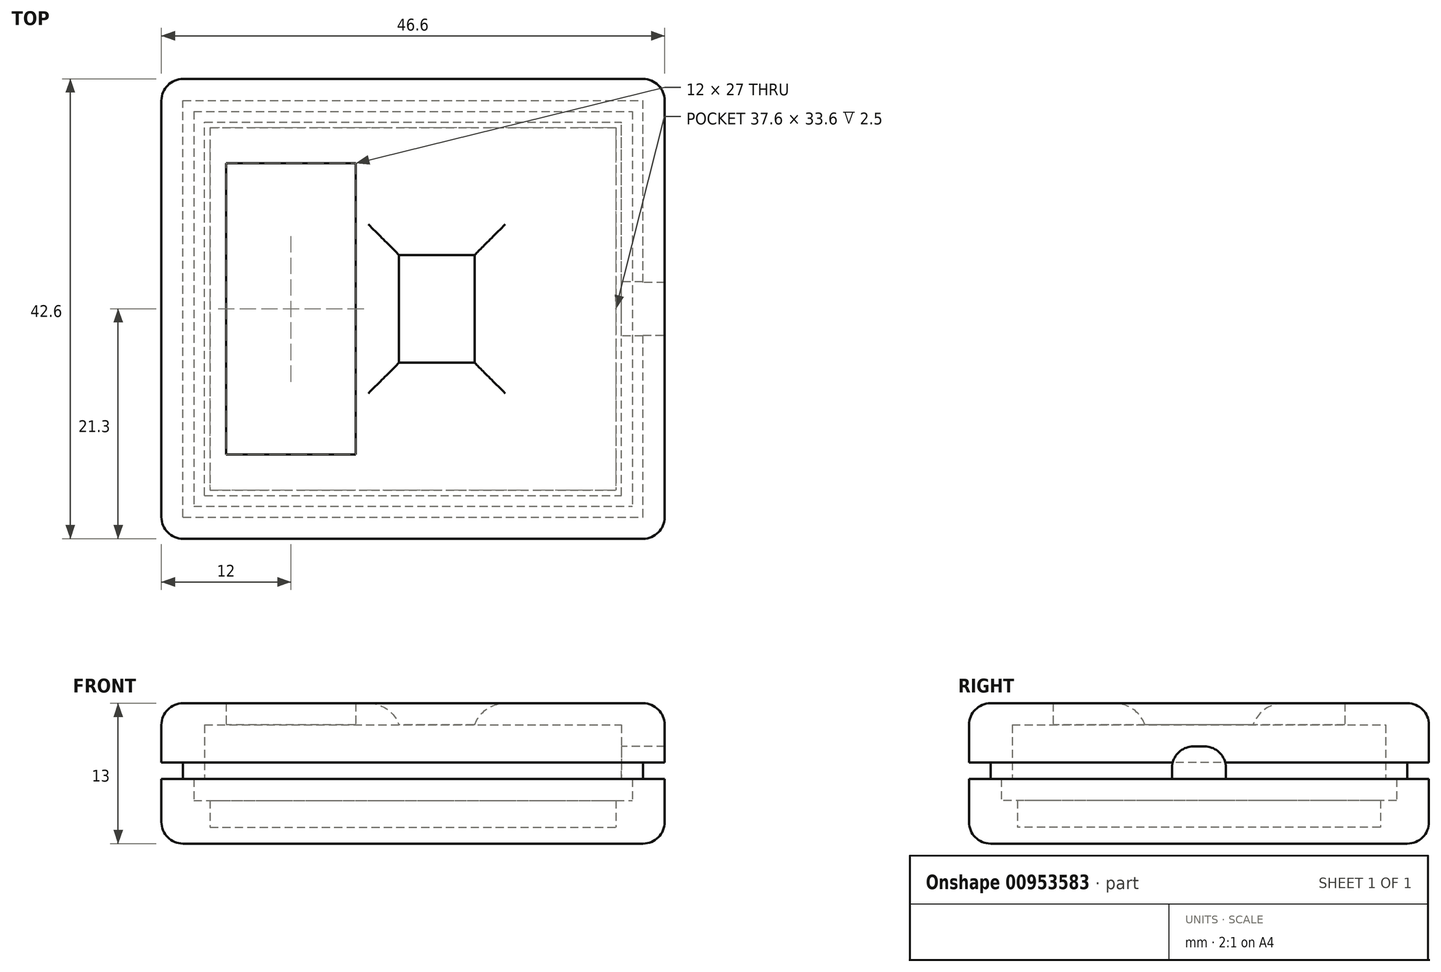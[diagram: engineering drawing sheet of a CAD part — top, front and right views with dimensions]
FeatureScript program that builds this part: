
annotation { "Feature Type Name" : "Feature", "Feature Type Description" : "" }
export const myFeature = defineFeature(function(context is Context, id is Id, definition is map)
    precondition{}
    {
        {
            assignVariable(context, id + "F0", {"name" : "HIGH", "anyValue" : 6 * mm});
        }
        {
            assignVariable(context, id + "F1", {"name" : "PCB_HIGH", "anyValue" : 2 * mm});
        }
        {
            var Q0;
            Q0=qCreatedBy(makeId("Top.planeOp"),FACE);
            var sketch = newSketch(context, id + "F2", { "sketchPlane" : qUnion([Q0])});
            skLineSegment(sketch, "E0.bottom", {"start": v(-23.3, 21.3) * mm, "end": v(23.3, 21.3) * mm});
            skLineSegment(sketch, "E0.top", {"start": v(-23.3, -21.3) * mm, "end": v(23.3, -21.3) * mm});
            skLineSegment(sketch, "E0.left", {"start": v(-23.3, 21.3) * mm, "end": v(-23.3, -21.3) * mm});
            skLineSegment(sketch, "E0.right", {"start": v(23.3, 21.3) * mm, "end": v(23.3, -21.3) * mm});
            skLineSegment(sketch, "E1", {"start": v(-23.3, 21.3) * mm, "end": v(23.3, -21.3) * mm, "construction": true});
            skLineSegment(sketch, "E2", {"start": v(23.3, 21.3) * mm, "end": v(-23.3, -21.3) * mm, "construction": true});
            skPoint(sketch, "E3", {"position": v(0, 0) * mm});
            skSolve(sketch);
        }
        {
            var Q0;
            Q0=qSketchRegion(id+"F2",true);
            extrude(context, id + "F3", {"entities" : qUnion([Q0]), "depth" : (getVariable(context, 'HIGH')), "offsetDistance" : 25 * mm});
        }
        {
            var Q0;
            Q0=qCreatedBy(makeId("Top.planeOp"),FACE);
            cPlane(context, id + "F4", {"entities" : qUnion([Q0]), "cplaneType" : CPlaneType.OFFSET, "offset" : 1.5 * mm, "width" : 150 * mm, "height" : 150 * mm});
        }
        {
            var Q0;
            Q0=qCreatedBy(id+"F4.planeOp",FACE);
            var sketch = newSketch(context, id + "F5", { "sketchPlane" : qUnion([Q0])});
            skLineSegment(sketch, "E4.bottom", {"start": v(-18.8, 16.8) * mm, "end": v(18.8, 16.8) * mm});
            skLineSegment(sketch, "E4.top", {"start": v(-18.8, -16.8) * mm, "end": v(18.8, -16.8) * mm});
            skLineSegment(sketch, "E4.left", {"start": v(-18.8, 16.8) * mm, "end": v(-18.8, -16.8) * mm});
            skLineSegment(sketch, "E4.right", {"start": v(18.8, 16.8) * mm, "end": v(18.8, -16.8) * mm});
            skSolve(sketch);
        }
        {
            var Q0;
            Q0=qSketchRegion(id+"F5",true);
            extrude(context, id + "F6", {"entities" : qUnion([Q0]), "operationType" : NewBodyOperationType.REMOVE, "depth" : (getVariable(context, 'HIGH') - 1.5 * mm), "offsetDistance" : 25 * mm});
        }
        {
            var Q0;
            Q0=qCreatedBy(makeId("Top.planeOp"),FACE);
            cPlane(context, id + "F7", {"entities" : qUnion([Q0]), "cplaneType" : CPlaneType.OFFSET, "offset" : (getVariable(context, 'HIGH') - getVariable(context, 'PCB_HIGH')), "width" : 150 * mm, "height" : 150 * mm});
        }
        {
            var Q0;
            Q0=qCreatedBy(id+"F7.planeOp",FACE);
            var sketch = newSketch(context, id + "F8", { "sketchPlane" : qUnion([Q0])});
            skLineSegment(sketch, "E5.bottom", {"start": v(-18.8, 16.8) * mm, "end": v(18.8, 16.8) * mm});
            skLineSegment(sketch, "E5.top", {"start": v(-18.8, -16.8) * mm, "end": v(18.8, -16.8) * mm});
            skLineSegment(sketch, "E5.left", {"start": v(-18.8, 16.8) * mm, "end": v(-18.8, -16.8) * mm});
            skLineSegment(sketch, "E5.right", {"start": v(18.8, 16.8) * mm, "end": v(18.8, -16.8) * mm});
            skLineSegment(sketch, "E6.bottom", {"start": v(-20.3, 18.3) * mm, "end": v(20.3, 18.3) * mm});
            skLineSegment(sketch, "E6.top", {"start": v(-20.3, -18.3) * mm, "end": v(20.3, -18.3) * mm});
            skLineSegment(sketch, "E6.left", {"start": v(-20.3, 18.3) * mm, "end": v(-20.3, -18.3) * mm});
            skLineSegment(sketch, "E6.right", {"start": v(20.3, 18.3) * mm, "end": v(20.3, -18.3) * mm});
            skSolve(sketch);
        }
        {
            var Q0;
            Q0=qSketchRegion(id+"F8",true);
            extrude(context, id + "F9", {"entities" : qUnion([Q0]), "operationType" : NewBodyOperationType.REMOVE, "depth" : (getVariable(context, 'PCB_HIGH')), "offsetDistance" : 25 * mm});
        }
        {
            var Q0;
            Q0=makeQuery(id+"F3.opExtrude","CAP_FACE",FACE,{"disambiguationData":[OSD([sQuery(id+"F2.wireOp",EDGE,"E0.bottom"),sQuery(id+"F2.wireOp",EDGE,"E0.top"),sQuery(id+"F2.wireOp",EDGE,"E0.left"),sQuery(id+"F2.wireOp",EDGE,"E0.right")])],"isStart":false});
            var sketch = newSketch(context, id + "F10", { "sketchPlane" : qUnion([Q0])});
            skLineSegment(sketch, "E7.bottom", {"start": v(-23.3, 21.3) * mm, "end": v(23.3, 21.3) * mm});
            skLineSegment(sketch, "E7.top", {"start": v(-23.3, -21.3) * mm, "end": v(23.3, -21.3) * mm});
            skLineSegment(sketch, "E7.left", {"start": v(-23.3, 21.3) * mm, "end": v(-23.3, -21.3) * mm});
            skLineSegment(sketch, "E7.right", {"start": v(23.3, 21.3) * mm, "end": v(23.3, -21.3) * mm});
            skLineSegment(sketch, "E8.bottom", {"start": v(-21.8, 19.8) * mm, "end": v(21.8, 19.8) * mm});
            skLineSegment(sketch, "E8.top", {"start": v(-21.8, -19.8) * mm, "end": v(21.8, -19.8) * mm});
            skLineSegment(sketch, "E8.left", {"start": v(-21.8, 19.8) * mm, "end": v(-21.8, -19.8) * mm});
            skLineSegment(sketch, "E8.right", {"start": v(21.8, 19.8) * mm, "end": v(21.8, -19.8) * mm});
            skSolve(sketch);
        }
        {
            var Q0;
            Q0 = qSketchRegion(id + "F10", true);
            extrude(context, id + "F11", {"entities" : qUnion([Q0]), "operationType" : NewBodyOperationType.ADD, "depth" : 1.5 * mm, "offsetDistance" : 25 * mm});
        }
        {
            var Q0;
            Q0=makeQuery(id+"F11.boolean.opBoolean","MERGE",EDGE,{"derivedFrom":[makeQuery(id+"F3.opExtrude","SWEPT_EDGE",EDGE,{"disambiguationData":[OSD([sQuery(id+"F2.wireOp",EDGE,"E0.bottom"),sQuery(id+"F2.wireOp",EDGE,"E0.left")])]}),makeQuery(id+"F11.opExtrude","SWEPT_EDGE",EDGE,{"disambiguationData":[OSD([sQuery(id+"F10.wireOp",EDGE,"E7.bottom"),sQuery(id+"F10.wireOp",EDGE,"E7.left")])]})]});
            var Q1;
            Q1=makeQuery(id+"F11.boolean.opBoolean","MERGE",EDGE,{"derivedFrom":[makeQuery(id+"F3.opExtrude","SWEPT_EDGE",EDGE,{"disambiguationData":[OSD([sQuery(id+"F2.wireOp",EDGE,"E0.top"),sQuery(id+"F2.wireOp",EDGE,"E0.left")])]}),makeQuery(id+"F11.opExtrude","SWEPT_EDGE",EDGE,{"disambiguationData":[OSD([sQuery(id+"F10.wireOp",EDGE,"E7.top"),sQuery(id+"F10.wireOp",EDGE,"E7.left")])]})]});
            var Q2;
            Q2=makeQuery(id+"F11.boolean.opBoolean","MERGE",EDGE,{"derivedFrom":[makeQuery(id+"F3.opExtrude","SWEPT_EDGE",EDGE,{"disambiguationData":[OSD([sQuery(id+"F2.wireOp",EDGE,"E0.bottom"),sQuery(id+"F2.wireOp",EDGE,"E0.right")])]}),makeQuery(id+"F11.opExtrude","SWEPT_EDGE",EDGE,{"disambiguationData":[OSD([sQuery(id+"F10.wireOp",EDGE,"E7.bottom"),sQuery(id+"F10.wireOp",EDGE,"E7.right")])]})]});
            var Q3;
            Q3=makeQuery(id+"F11.boolean.opBoolean","MERGE",EDGE,{"derivedFrom":[makeQuery(id+"F3.opExtrude","SWEPT_EDGE",EDGE,{"disambiguationData":[OSD([sQuery(id+"F2.wireOp",EDGE,"E0.top"),sQuery(id+"F2.wireOp",EDGE,"E0.right")])]}),makeQuery(id+"F11.opExtrude","SWEPT_EDGE",EDGE,{"disambiguationData":[OSD([sQuery(id+"F10.wireOp",EDGE,"E7.top"),sQuery(id+"F10.wireOp",EDGE,"E7.right")])]})]});
            fillet(context, id + "F12", {"entities" : qUnion([Q0, Q1, Q2, Q3]), "radius" : 2 * mm, "tangentPropagation" : true, "allowEdgeOverflow" : false});
        }
        {
            var Q0;
            Q0=makeQuery(id+"F11.opExtrude","CAP_FACE",FACE,{"disambiguationData":[OSD([sQuery(id+"F10.wireOp",EDGE,"E7.bottom"),sQuery(id+"F10.wireOp",EDGE,"E7.top"),sQuery(id+"F10.wireOp",EDGE,"E7.left"),sQuery(id+"F10.wireOp",EDGE,"E7.right"),sQuery(id+"F10.wireOp",EDGE,"E8.bottom"),sQuery(id+"F10.wireOp",EDGE,"E8.top"),sQuery(id+"F10.wireOp",EDGE,"E8.left"),sQuery(id+"F10.wireOp",EDGE,"E8.right")])],"isStart":false});
            var sketch = newSketch(context, id + "F13", { "sketchPlane" : qUnion([Q0])});
            skLineSegment(sketch, "E9.bottom", {"start": v(21.8, 2.5) * mm, "end": v(23.3, 2.5) * mm});
            skLineSegment(sketch, "E9.top", {"start": v(21.8, -2.5) * mm, "end": v(23.3, -2.5) * mm});
            skLineSegment(sketch, "E9.left", {"start": v(21.8, 2.5) * mm, "end": v(21.8, -2.5) * mm});
            skLineSegment(sketch, "E9.right", {"start": v(23.3, 2.5) * mm, "end": v(23.3, -2.5) * mm});
            skLineSegment(sketch, "E10", {"start": v(-25.81, 0) * mm, "end": v(25.62, 0) * mm, "construction": true});
            skPoint(sketch, "E10.endSnap0", {"position": v(23.3, 0) * mm});
            skSolve(sketch);
        }
        {
            var Q0;
            Q0 = qSketchRegion(id + "F13", true);
            extrude(context, id + "F14", {"entities" : qUnion([Q0]), "operationType" : NewBodyOperationType.REMOVE, "oppositeDirection" : true, "depth" : 1.5 * mm, "offsetDistance" : 25 * mm});
        }
        {
            var Q0;
            Q0=makeQuery(id+"F14.boolean.opBoolean","COPY",EDGE,{"derivedFrom":makeQuery(id+"F14.opExtrude","CAP_EDGE",EDGE,{"disambiguationData":[OSD([sQuery(id+"F13.wireOp",EDGE,"E9.top")])],"isStart":false})});
            var Q1;
            Q1=makeQuery(id+"F14.boolean.opBoolean","COPY",EDGE,{"derivedFrom":makeQuery(id+"F14.opExtrude","CAP_EDGE",EDGE,{"disambiguationData":[OSD([sQuery(id+"F13.wireOp",EDGE,"E9.bottom")])],"isStart":false})});
            fillet(context, id + "F15", {"entities" : qUnion([Q0, Q1]), "radius" : 2 * mm, "tangentPropagation" : true, "allowEdgeOverflow" : false});
        }
        {
            var Q0;
            Q0=makeQuery(id+"F3.opExtrude","CAP_EDGE",EDGE,{"disambiguationData":[OSD([sQuery(id+"F2.wireOp",EDGE,"E0.left")])],"isStart":true});
            fillet(context, id + "F16", {"entities" : qUnion([Q0]), "radius" : 2 * mm, "tangentPropagation" : true, "allowEdgeOverflow" : false});
        }
        {
            var Q0;
            Q0=makeQuery(id+"F3.opExtrude","CAP_FACE",FACE,{"disambiguationData":[OSD([sQuery(id+"F2.wireOp",EDGE,"E0.bottom"),sQuery(id+"F2.wireOp",EDGE,"E0.top"),sQuery(id+"F2.wireOp",EDGE,"E0.left"),sQuery(id+"F2.wireOp",EDGE,"E0.right")])],"isStart":false});
            cPlane(context, id + "F17", {"entities" : qUnion([Q0]), "cplaneType" : CPlaneType.OFFSET, "offset" : 0 * mm, "width" : 150 * mm, "height" : 150 * mm});
        }
        {
            var Q0;
            Q0=qCreatedBy(id+"F17.planeOp",FACE);
            var sketch = newSketch(context, id + "F18", { "sketchPlane" : qUnion([Q0])});
            skLineSegment(sketch, "E11.bottom", {"start": v(-23.3, 21.3) * mm, "end": v(23.3, 21.3) * mm});
            skLineSegment(sketch, "E11.top", {"start": v(-23.3, -21.3) * mm, "end": v(23.3, -21.3) * mm});
            skLineSegment(sketch, "E11.left", {"start": v(-23.3, 21.3) * mm, "end": v(-23.3, -21.3) * mm});
            skLineSegment(sketch, "E11.right", {"start": v(23.3, 21.3) * mm, "end": v(23.3, -21.3) * mm});
            skSolve(sketch);
        }
        {
            var Q0;
            Q0=qSketchRegion(id+"F18",true);
            extrude(context, id + "F19", {"entities" : qUnion([Q0]), "depth" : (5 + 2) * mm, "offsetDistance" : 25 * mm});
        }
        {
            var Q0;
            Q0=qCreatedBy(id+"F17.planeOp",FACE);
            var sketch = newSketch(context, id + "F20", { "sketchPlane" : qUnion([Q0])});
            skLineSegment(sketch, "E12.bottom", {"start": v(-19.3, -17.3) * mm, "end": v(19.3, -17.3) * mm});
            skLineSegment(sketch, "E12.top", {"start": v(-19.3, 17.3) * mm, "end": v(19.3, 17.3) * mm});
            skLineSegment(sketch, "E12.left", {"start": v(-19.3, -17.3) * mm, "end": v(-19.3, 17.3) * mm});
            skLineSegment(sketch, "E12.right", {"start": v(19.3, -17.3) * mm, "end": v(19.3, 17.3) * mm});
            skSolve(sketch);
        }
        {
            var Q0;
            Q0=qSketchRegion(id+"F20",true);
            extrude(context, id + "F21", {"entities" : qUnion([Q0]), "operationType" : NewBodyOperationType.REMOVE, "depth" : 5 * mm, "offsetDistance" : 25 * mm});
        }
        {
            var Q0;
            Q0=makeQuery(id+"F19.opExtrude","CAP_FACE",FACE,{"disambiguationData":[OSD([sQuery(id+"F18.wireOp",EDGE,"E11.bottom"),sQuery(id+"F18.wireOp",EDGE,"E11.top"),sQuery(id+"F18.wireOp",EDGE,"E11.left"),sQuery(id+"F18.wireOp",EDGE,"E11.right")])],"isStart":true});
            var sketch = newSketch(context, id + "F22", { "sketchPlane" : qUnion([Q0])});
            skLineSegment(sketch, "E13.bottom", {"start": v(-21.3, 19.3) * mm, "end": v(21.3, 19.3) * mm});
            skLineSegment(sketch, "E13.top", {"start": v(-21.3, -19.3) * mm, "end": v(21.3, -19.3) * mm});
            skLineSegment(sketch, "E13.left", {"start": v(-21.3, 19.3) * mm, "end": v(-21.3, -19.3) * mm});
            skLineSegment(sketch, "E13.right", {"start": v(21.3, 19.3) * mm, "end": v(21.3, -19.3) * mm});
            skLineSegment(sketch, "E14.bottom", {"start": v(-23.3, 21.3) * mm, "end": v(23.3, 21.3) * mm});
            skLineSegment(sketch, "E14.top", {"start": v(-23.3, -21.3) * mm, "end": v(23.3, -21.3) * mm});
            skLineSegment(sketch, "E14.left", {"start": v(-23.3, 21.3) * mm, "end": v(-23.3, -21.3) * mm});
            skLineSegment(sketch, "E14.right", {"start": v(23.3, 21.3) * mm, "end": v(23.3, -21.3) * mm});
            skSolve(sketch);
        }
        {
            var Q0;
            Q0 = qSketchRegion(id + "F22", true);
            extrude(context, id + "F23", {"entities" : qUnion([Q0]), "operationType" : NewBodyOperationType.REMOVE, "oppositeDirection" : true, "depth" : 1.5 * mm, "offsetDistance" : 25 * mm});
        }
        {
            var Q0;
            Q0=qCreatedBy(id+"F17.planeOp",FACE);
            var sketch = newSketch(context, id + "F24", { "sketchPlane" : qUnion([Q0])});
            skLineSegment(sketch, "E15", {"start": v(-59.85, 0) * mm, "end": v(56.97, 0) * mm, "construction": true});
            skLineSegment(sketch, "E16.bottom", {"start": v(23.3, 2.5) * mm, "end": v(18.3, 2.5) * mm});
            skLineSegment(sketch, "E16.top", {"start": v(23.3, -2.5) * mm, "end": v(18.3, -2.5) * mm});
            skLineSegment(sketch, "E16.left", {"start": v(23.3, 2.5) * mm, "end": v(23.3, -2.5) * mm});
            skLineSegment(sketch, "E16.right", {"start": v(18.3, 2.5) * mm, "end": v(18.3, -2.5) * mm});
            skSolve(sketch);
        }
        {
            var Q0;
            Q0 = qSketchRegion(id + "F24", true);
            extrude(context, id + "F25", {"entities" : qUnion([Q0]), "operationType" : NewBodyOperationType.REMOVE, "depth" : 3 * mm, "offsetDistance" : 25 * mm});
        }
        {
            var Q0;
            Q0=makeQuery(id+"F25.boolean.opBoolean","COPY",EDGE,{"derivedFrom":makeQuery(id+"F25.opExtrude","CAP_EDGE",EDGE,{"disambiguationData":[OSD([sQuery(id+"F24.wireOp",EDGE,"E16.bottom")])],"isStart":false})});
            var Q1;
            Q1=makeQuery(id+"F25.boolean.opBoolean","COPY",EDGE,{"derivedFrom":makeQuery(id+"F25.opExtrude","CAP_EDGE",EDGE,{"disambiguationData":[OSD([sQuery(id+"F24.wireOp",EDGE,"E16.top")])],"isStart":false})});
            fillet(context, id + "F26", {"entities" : qUnion([Q0, Q1]), "radius" : 2 * mm, "tangentPropagation" : true, "allowEdgeOverflow" : false});
        }
        {
            var Q0;
            Q0=qCreatedBy(id+"F17.planeOp",FACE);
            var sketch = newSketch(context, id + "F27", { "sketchPlane" : qUnion([Q0])});
            skLineSegment(sketch, "E17", {"start": v(-28.9, 0) * mm, "end": v(28.59, 0) * mm, "construction": true});
            skLineSegment(sketch, "E18.bottom", {"start": v(-1.3, -5) * mm, "end": v(5.7, -5) * mm});
            skLineSegment(sketch, "E18.top", {"start": v(-1.3, 5) * mm, "end": v(5.7, 5) * mm});
            skLineSegment(sketch, "E18.left", {"start": v(-1.3, -5) * mm, "end": v(-1.3, 5) * mm});
            skLineSegment(sketch, "E18.right", {"start": v(5.7, -5) * mm, "end": v(5.7, 5) * mm});
            skLineSegment(sketch, "E19.bottom", {"start": v(-17.3, -13.5) * mm, "end": v(-5.3, -13.5) * mm});
            skLineSegment(sketch, "E19.top", {"start": v(-17.3, 13.5) * mm, "end": v(-5.3, 13.5) * mm});
            skLineSegment(sketch, "E19.left", {"start": v(-17.3, -13.5) * mm, "end": v(-17.3, 13.5) * mm});
            skLineSegment(sketch, "E19.right", {"start": v(-5.3, -13.5) * mm, "end": v(-5.3, 13.5) * mm});
            skSolve(sketch);
        }
        {
            var Q0;
            Q0 = qSketchRegion(id + "F27", true);
            extrude(context, id + "F28", {"entities" : qUnion([Q0]), "operationType" : NewBodyOperationType.REMOVE, "depth" : 9.4 * mm, "offsetDistance" : 25 * mm});
        }
        {
            var Q0;
            Q0=makeQuery(id+"F19.opExtrude","SWEPT_EDGE",EDGE,{"disambiguationData":[OSD([sQuery(id+"F18.wireOp",EDGE,"E11.top"),sQuery(id+"F18.wireOp",EDGE,"E11.left")])]});
            var Q1;
            Q1=makeQuery(id+"F19.opExtrude","SWEPT_EDGE",EDGE,{"disambiguationData":[OSD([sQuery(id+"F18.wireOp",EDGE,"E11.top"),sQuery(id+"F18.wireOp",EDGE,"E11.right")])]});
            var Q2;
            Q2=makeQuery(id+"F19.opExtrude","SWEPT_EDGE",EDGE,{"disambiguationData":[OSD([sQuery(id+"F18.wireOp",EDGE,"E11.bottom"),sQuery(id+"F18.wireOp",EDGE,"E11.right")])]});
            var Q3;
            Q3=makeQuery(id+"F19.opExtrude","SWEPT_EDGE",EDGE,{"disambiguationData":[OSD([sQuery(id+"F18.wireOp",EDGE,"E11.bottom"),sQuery(id+"F18.wireOp",EDGE,"E11.left")])]});
            fillet(context, id + "F29", {"entities" : qUnion([Q0, Q1, Q2, Q3]), "radius" : 2 * mm, "tangentPropagation" : true, "allowEdgeOverflow" : false});
        }
        {
            var Q0;
            Q0=makeQuery(id+"F19.opExtrude","CAP_EDGE",EDGE,{"disambiguationData":[OSD([sQuery(id+"F18.wireOp",EDGE,"E11.right")])],"isStart":false});
            fillet(context, id + "F30", {"entities" : qUnion([Q0]), "radius" : 2 * mm, "tangentPropagation" : true, "allowEdgeOverflow" : false});
        }
        {
            var Q0;
            Q0=makeQuery(id+"F28.boolean.opBoolean","INTERSECT",EDGE,{"derivedFrom":[makeQuery(id+"F19.opExtrude","CAP_FACE",FACE,{"disambiguationData":[OSD([sQuery(id+"F18.wireOp",EDGE,"E11.bottom"),sQuery(id+"F18.wireOp",EDGE,"E11.top"),sQuery(id+"F18.wireOp",EDGE,"E11.left"),sQuery(id+"F18.wireOp",EDGE,"E11.right")])],"isStart":false}),makeQuery(id+"F28.opExtrude","SWEPT_FACE",FACE,{"disambiguationData":[OSD([sQuery(id+"F27.wireOp",EDGE,"E18.top")])]})]});
            var Q1;
            Q1=makeQuery(id+"F28.boolean.opBoolean","INTERSECT",EDGE,{"derivedFrom":[makeQuery(id+"F19.opExtrude","CAP_FACE",FACE,{"disambiguationData":[OSD([sQuery(id+"F18.wireOp",EDGE,"E11.bottom"),sQuery(id+"F18.wireOp",EDGE,"E11.top"),sQuery(id+"F18.wireOp",EDGE,"E11.left"),sQuery(id+"F18.wireOp",EDGE,"E11.right")])],"isStart":false}),makeQuery(id+"F28.opExtrude","SWEPT_FACE",FACE,{"disambiguationData":[OSD([sQuery(id+"F27.wireOp",EDGE,"E18.right")])]})]});
            var Q2;
            Q2=makeQuery(id+"F28.boolean.opBoolean","INTERSECT",EDGE,{"derivedFrom":[makeQuery(id+"F19.opExtrude","CAP_FACE",FACE,{"disambiguationData":[OSD([sQuery(id+"F18.wireOp",EDGE,"E11.bottom"),sQuery(id+"F18.wireOp",EDGE,"E11.top"),sQuery(id+"F18.wireOp",EDGE,"E11.left"),sQuery(id+"F18.wireOp",EDGE,"E11.right")])],"isStart":false}),makeQuery(id+"F28.opExtrude","SWEPT_FACE",FACE,{"disambiguationData":[OSD([sQuery(id+"F27.wireOp",EDGE,"E18.left")])]})]});
            var Q3;
            Q3=makeQuery(id+"F28.boolean.opBoolean","INTERSECT",EDGE,{"derivedFrom":[makeQuery(id+"F19.opExtrude","CAP_FACE",FACE,{"disambiguationData":[OSD([sQuery(id+"F18.wireOp",EDGE,"E11.bottom"),sQuery(id+"F18.wireOp",EDGE,"E11.top"),sQuery(id+"F18.wireOp",EDGE,"E11.left"),sQuery(id+"F18.wireOp",EDGE,"E11.right")])],"isStart":false}),makeQuery(id+"F28.opExtrude","SWEPT_FACE",FACE,{"disambiguationData":[OSD([sQuery(id+"F27.wireOp",EDGE,"E18.bottom")])]})]});
            fillet(context, id + "F31", {"entities" : qUnion([Q0, Q1, Q2, Q3]), "radius" : 3 * mm, "tangentPropagation" : true, "allowEdgeOverflow" : false});
        }
    });
